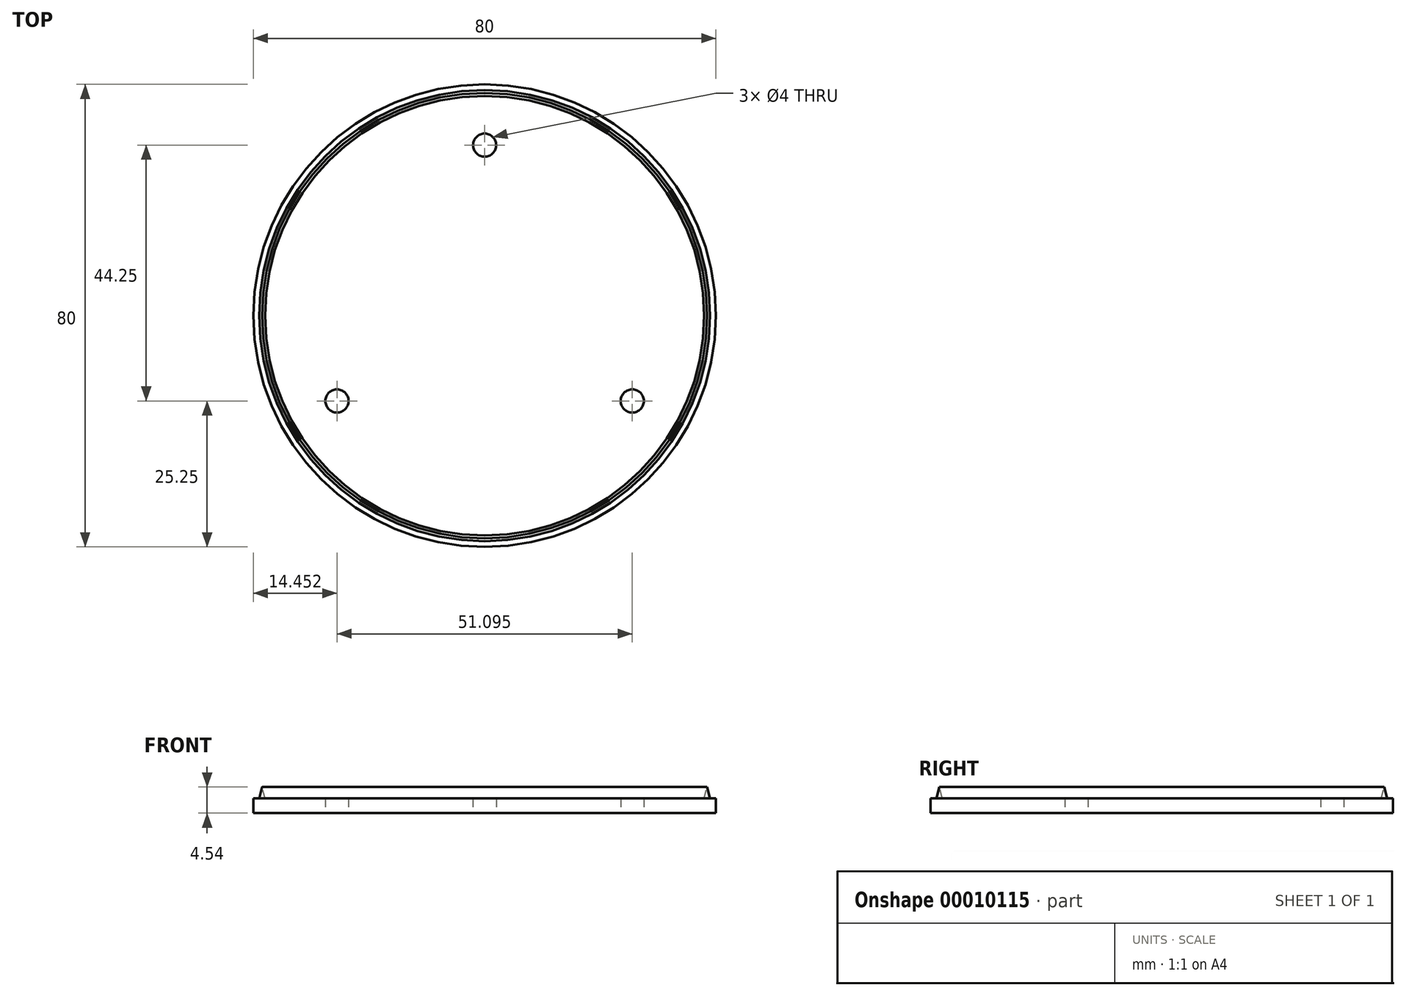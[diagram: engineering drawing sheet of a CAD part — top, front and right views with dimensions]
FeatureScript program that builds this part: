
annotation { "Feature Type Name" : "Feature", "Feature Type Description" : "" }
export const myFeature = defineFeature(function(context is Context, id is Id, definition is map)
    precondition{}
    {
        {
            var Q0;
            Q0=qCreatedBy(makeId("Top.planeOp"),FACE);
            var sketch = newSketch(context, id + "F0", { "sketchPlane" : qUnion([Q0])});
            skCircle(sketch, "E0", {"center": v(0, 0) * mm, "radius": 40 * mm});
            skCircle(sketch, "E1", {"center": v(0, 29.5) * mm, "radius": 2 * mm});
            skLineSegment(sketch, "E2", {"start": v(0, 0) * mm, "end": v(0, 29.5) * mm, "construction": true});
            skLineSegment(sketch, "E3.1.0", {"start": v(0, 0) * mm, "end": v(-25.55, -14.75) * mm, "construction": true});
            skCircle(sketch, "E3.1.1", {"center": v(-25.55, -14.75) * mm, "radius": 2 * mm});
            skLineSegment(sketch, "E3.2.0", {"start": v(0, 0) * mm, "end": v(25.55, -14.75) * mm, "construction": true});
            skCircle(sketch, "E3.2.1", {"center": v(25.55, -14.75) * mm, "radius": 2 * mm});
            skLineSegment(sketch, "E4", {"start": v(0, 29.5) * mm, "end": v(0, 40) * mm, "construction": true});
            skSolve(sketch);
        }
        {
            var Q0;
            Q0=makeQuery(id+"F0.imprint","IMPRINT",FACE,{"disambiguationData":[TD([[makeQuery(id+"F0.imprint","IMPRINT",EDGE,{"derivedFrom":sQuery(id+"F0.wireOp",EDGE,"E0")}),1.0]])]});
            extrude(context, id + "F1", {"entities" : qUnion([Q0]), "depth" : 2.54 * mm});
        }
        {
            var Q0;
            Q0=qCreatedBy(makeId("Front.planeOp"),FACE);
            var sketch = newSketch(context, id + "F2", { "sketchPlane" : qUnion([Q0])});
            skLineSegment(sketch, "E5", {"start": v(-39, 2.54) * mm, "end": v(-38.5, 4.54) * mm});
            skLineSegment(sketch, "E6", {"start": v(-38.5, 4.54) * mm, "end": v(-38, 2.54) * mm});
            skLineSegment(sketch, "E7", {"start": v(-38, 2.54) * mm, "end": v(-39, 2.54) * mm});
            skSolve(sketch);
        }
        {
            var Q0;
            Q0 = qSketchRegion(id + "F2", true);
            var Q1;
            Q1=makeQuery(id+"F1.opExtrude","CAP_EDGE",EDGE,{"disambiguationData":[OSD([sQuery(id+"F0.wireOp",EDGE,"E0")])],"isStart":false});
            sweep(context, id + "F3", {"operationType" : NewBodyOperationType.ADD, "profiles" : qUnion([Q0]), "path" : qUnion([Q1])});
        }
    });
